# Revit family: LumiWall 40 Outside Corner new new
name_source: partatom
category: Windows
revit_build: Autodesk Revit Architecture 2015 (Build: 20160512_1515(x64)
units: mm (PartAtom-declared; Revit-internal decimal feet)

## types (1)
- LumiWall 40
    C Center Panels = 28
    C Stacks = 2
    C Width = 49' - 8 3/16"
    Center = Yes
    Center 3P = No
    Center Panels = 28
    Default Sill Height = 3' - 0"
    Description = 40mm Multiwall Polycarbonate Vertical Translucent Panel System
    Frame Finish = Aluminum-Wasco-Clear_Anodized
    Height = 50' - 0"
    Left End = Yes
    Manufacturer = Wasco Skylights
    Model = LumiWall 40
    Panel Finish = Polycarbonate-Wasco-Clear
    Panel Length Note = Max 8' unsupported, sill to head. Over 8' requires intermediate panel clips with a max spacing of 78” frame to clip or clip to clip. Note: horizontal support for panel clips – not by Wasco.
    Panel Width = 1' - 7 175/256"
    Product Documentation Link = Contact Manufacturer
    Product Name = LumiWall 40
    Product Page URL = http://www.wascoskylights.com
    Right End = Yes
    Single Panel = No
    Stack Length = 24' - 0"
    Stack Width = 49' - 2 161/256"
    Stacks = 2
    Stacks Note = Must have Stack option selected for all windows with Height over 25'
    Subsill Note = Optional but recommended; required if Unit Width is 24'or more and if splice is used.
    Thermal Performance = Offers optional polyurethane thermal breaks for improved thermal performance
    URL = http://www.wascoskylights.com
    Unit Height Note = Max height 25′ without stack joint. Unlimited height with stack joints
    Unit Width Note = Unrestricted, splice detail required every 24 ft.
    Wall Closure = By host
    Width = 50' - 0"

## geometry (parser evidence)
native form markers: Sweep x11
no freeform markers — native parametric forms only
